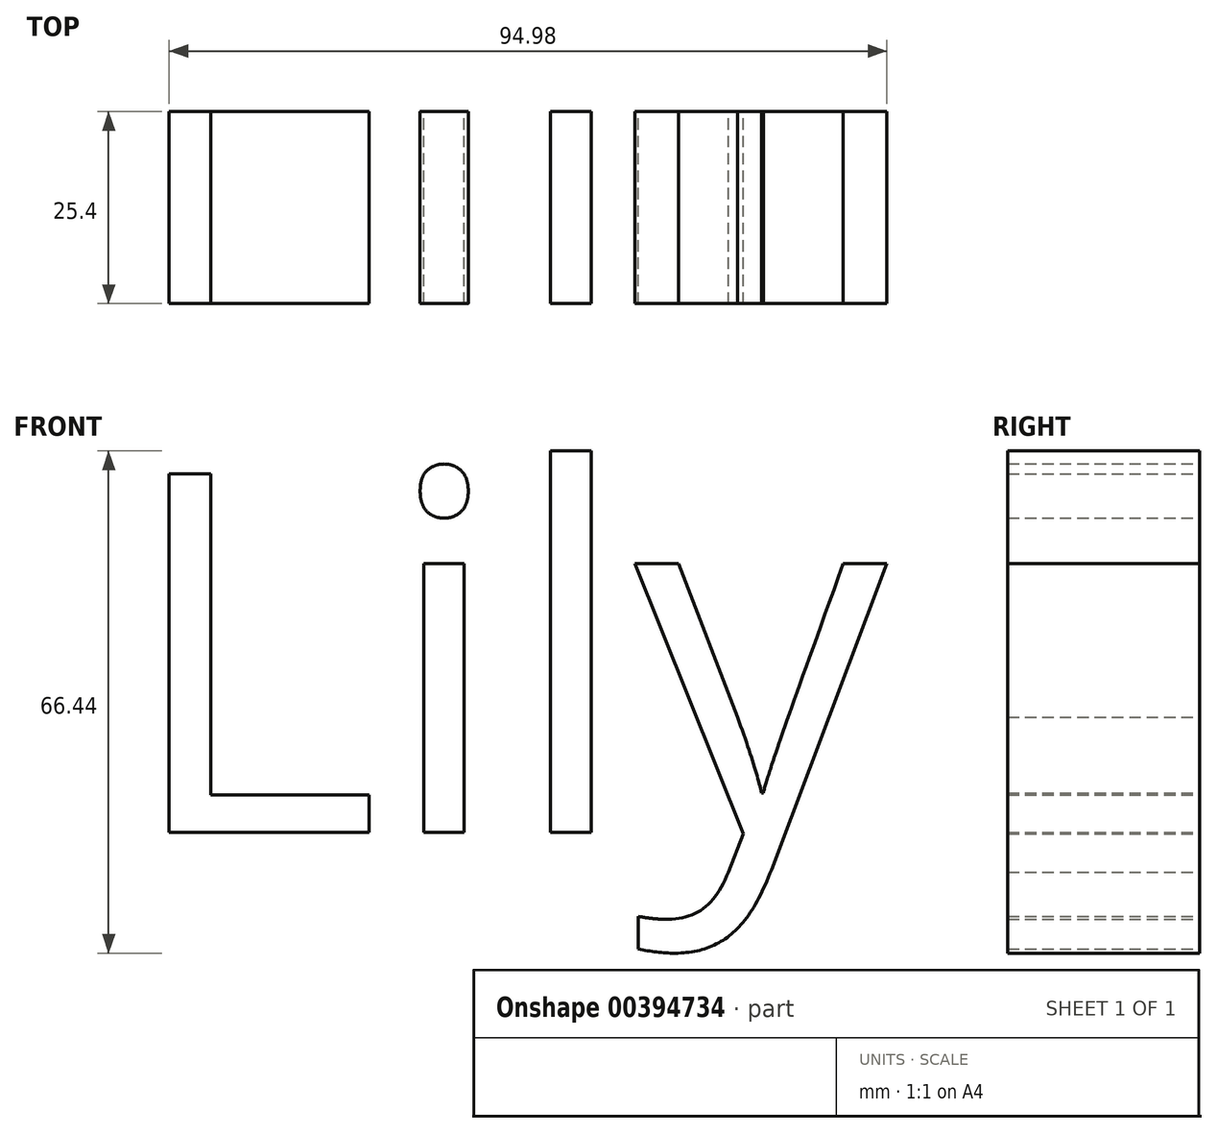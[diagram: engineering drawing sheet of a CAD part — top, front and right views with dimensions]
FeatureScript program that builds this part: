
annotation { "Feature Type Name" : "Feature", "Feature Type Description" : "" }
export const myFeature = defineFeature(function(context is Context, id is Id, definition is map)
    precondition{}
    {
        {
            var Q0;
            Q0=qCreatedBy(makeId("Front.planeOp"),FACE);
            var sketch = newSketch(context, id + "F0", { "sketchPlane" : qUnion([Q0])});
            skText(sketch, "E0", { "text": "Lily\n", "fontName": "OpenSans-Regular.ttf"});
            const initialGuessF0  = {"E0": [-0.039, -0.01975, 1, 0, 0.04783]};
            skSetInitialGuess(sketch, initialGuessF0);
            skSolve(sketch);
        }
        {
            var Q0;
            Q0 = qSketchRegion(id + "F0", true);
            extrude(context, id + "F1", {"entities" : qUnion([Q0]), "depth" : 25.4 * mm});
        }
    });
